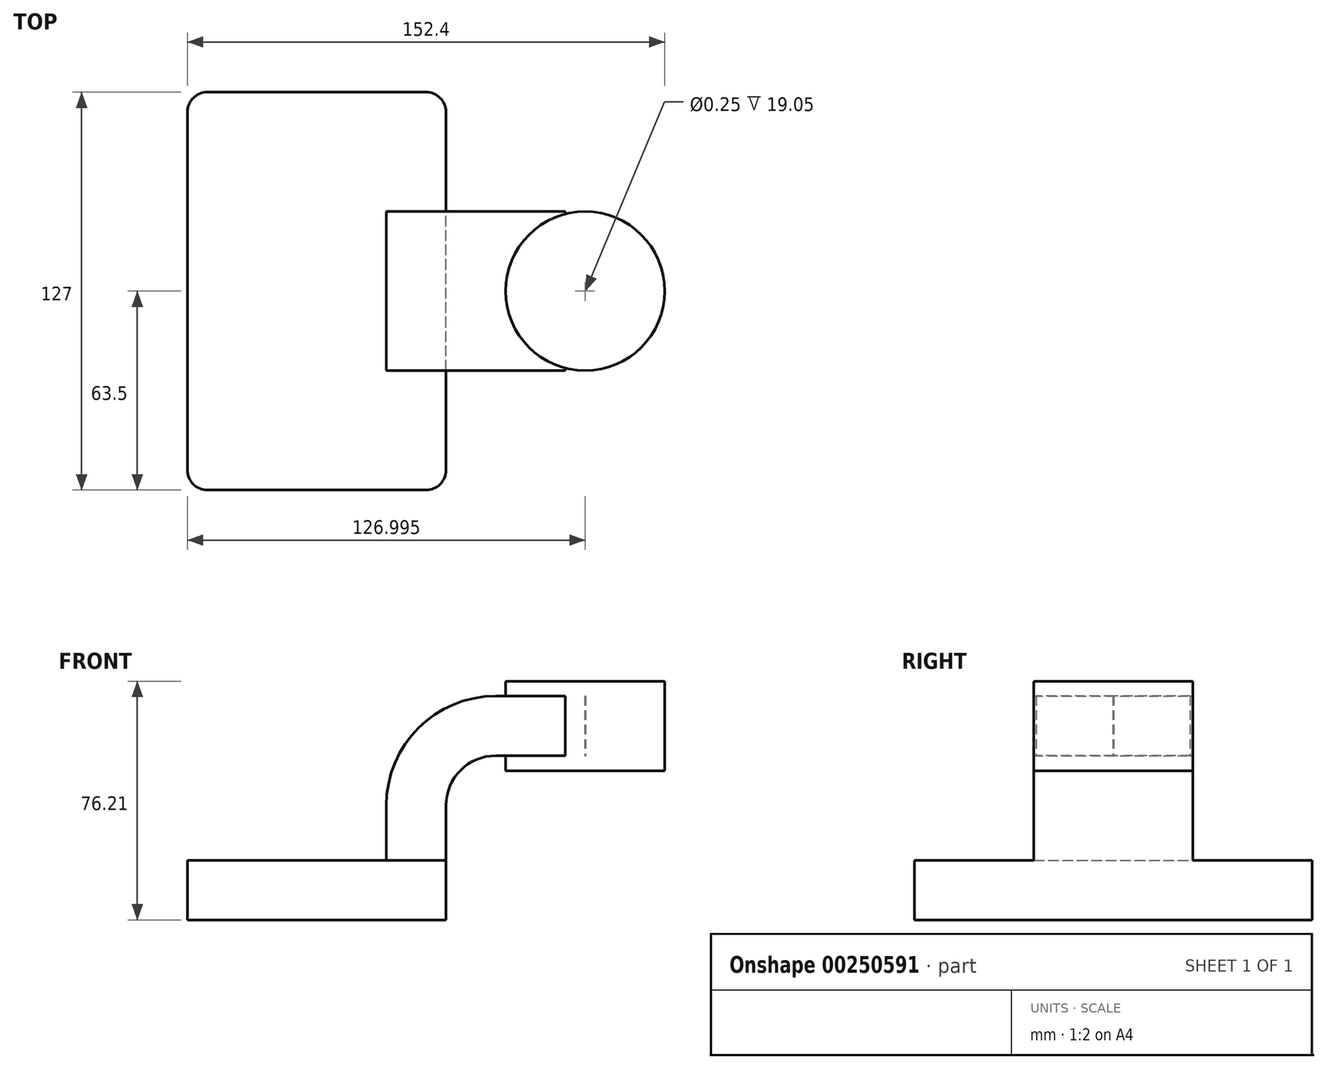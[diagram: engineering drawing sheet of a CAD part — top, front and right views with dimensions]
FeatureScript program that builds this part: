
annotation { "Feature Type Name" : "Feature", "Feature Type Description" : "" }
export const myFeature = defineFeature(function(context is Context, id is Id, definition is map)
    precondition{}
    {
        {
            var Q0;
            Q0=qCreatedBy(makeId("Front.planeOp"),FACE);
            var sketch = newSketch(context, id + "F0", { "sketchPlane" : qUnion([Q0])});
            skLineSegment(sketch, "E0.bottom", {"start": v(41.27, 9.53) * mm, "end": v(-41.28, 9.53) * mm});
            skLineSegment(sketch, "E0.top", {"start": v(41.28, -9.52) * mm, "end": v(-41.27, -9.52) * mm});
            skLineSegment(sketch, "E0.left", {"start": v(41.28, 9.53) * mm, "end": v(41.28, -9.52) * mm});
            skLineSegment(sketch, "E0.right", {"start": v(-41.28, 9.53) * mm, "end": v(-41.27, -9.52) * mm});
            skPoint(sketch, "E0.middle", {"position": v(0, 0) * mm});
            skLineSegment(sketch, "E1.bottom", {"start": v(111.12, 66.68) * mm, "end": v(60.32, 66.68) * mm});
            skLineSegment(sketch, "E1.top", {"start": v(111.12, 38.1) * mm, "end": v(60.33, 38.1) * mm});
            skLineSegment(sketch, "E1.left", {"start": v(111.12, 66.68) * mm, "end": v(111.12, 38.1) * mm});
            skLineSegment(sketch, "E1.right", {"start": v(60.32, 66.68) * mm, "end": v(60.33, 38.1) * mm});
            skPoint(sketch, "E1.middle", {"position": v(85.73, 52.39) * mm});
            skLineSegment(sketch, "E2", {"start": v(41.27, 9.53) * mm, "end": v(41.27, 27) * mm});
            skArc(sketch, "E3", {"start": v(41.27, 27) * mm, "mid": v(45.92, 38.23) * mm, "end": v(57.15, 42.88) * mm});
            skLineSegment(sketch, "E4", {"start": v(57.15, 42.88) * mm, "end": v(85.85, 42.88) * mm});
            skLineSegment(sketch, "E5.0", {"start": v(57.15, 61.93) * mm, "end": v(85.85, 61.93) * mm});
            skArc(sketch, "E5.1", {"start": v(22.23, 27) * mm, "mid": v(32.45, 51.7) * mm, "end": v(57.15, 61.93) * mm});
            skLineSegment(sketch, "E5.2", {"start": v(22.23, 9.53) * mm, "end": v(22.23, 27) * mm});
            skLineSegment(sketch, "E6", {"start": v(85.85, 42.88) * mm, "end": v(85.85, 61.93) * mm});
            skFitSpline(sketch, "E7", {"points": [v(-41.28, 9.52) * mm, v(57.15, 61.93) * mm], "startDerivative": vector(3.53, 68.47) * mm, "endDerivative": vector(154.22, 0.04) * mm});
            skLineSegment(sketch, "E8", {"start": v(85.72, 38.1) * mm, "end": v(85.72, 66.68) * mm});
            skSolve(sketch);
        }
        {
            var Q0;
            Q0=makeQuery(id+"F0.imprint","IMPRINT",FACE,{"disambiguationData":[TD([[makeQuery(id+"F0.imprint","IMPRINT",EDGE,{"derivedFrom":sQuery(id+"F0.wireOp",EDGE,"E0.top")}),-1.0]])]});
            extrude(context, id + "F1", {"entities" : qUnion([Q0]), "endBound" : BoundingType.SYMMETRIC, "depth" : 127 * mm});
        }
        {
            var Q0;
            {var subQ1=sQuery(id+"F0.wireOp",EDGE,"E2");Q0=makeQuery(id+"F0.imprint","IMPRINT",FACE,{"disambiguationData":[TD([[makeQuery(id+"F0.imprint","IMPRINT",EDGE,{"derivedFrom":subQ1}),1.0]])]});}
            extrude(context, id + "F2", {"entities" : qUnion([Q0]), "operationType" : NewBodyOperationType.ADD, "endBound" : BoundingType.SYMMETRIC, "depth" : 50.8 * mm});
        }
        {
            var Q0;
            Q0=makeQuery(id+"F0.imprint","IMPRINT",FACE,{"disambiguationData":[TD([[makeQuery(id+"F0.imprint","IMPRINT",EDGE,{"derivedFrom":sQuery(id+"F0.wireOp",EDGE,"E5.1")}),1.0]])]});
            extrude(context, id + "F3", {"entities" : qUnion([Q0]), "operationType" : NewBodyOperationType.ADD, "endBound" : BoundingType.SYMMETRIC, "depth" : 15.88 * mm});
        }
        {
            var Q0;
            Q0=makeQuery(id+"F1.opExtrude","CAP_EDGE",EDGE,{"disambiguationData":[OSD([sQuery(id+"F0.wireOp",EDGE,"E0.left")])],"isStart":false});
            var Q1;
            Q1=makeQuery(id+"F1.opExtrude","CAP_EDGE",EDGE,{"disambiguationData":[OSD([sQuery(id+"F0.wireOp",EDGE,"E0.right")])],"isStart":false});
            var Q2;
            Q2=makeQuery(id+"F1.opExtrude","CAP_EDGE",EDGE,{"disambiguationData":[OSD([sQuery(id+"F0.wireOp",EDGE,"E0.left")])],"isStart":true});
            var Q3;
            Q3=makeQuery(id+"F1.opExtrude","CAP_EDGE",EDGE,{"disambiguationData":[OSD([sQuery(id+"F0.wireOp",EDGE,"E0.right")])],"isStart":true});
            fillet(context, id + "F4", {"entities" : qUnion([Q0, Q1, Q2, Q3]), "radius" : 6.35 * mm, "tangentPropagation" : true, "allowEdgeOverflow" : false});
        }
        {
            var Q0;
            Q0=makeQuery(id+"F2.opExtrude","SWEPT_FACE",FACE,{"disambiguationData":[OSD([sQuery(id+"F0.wireOp",EDGE,"E1.right")])]});
            extrude(context, id + "F5", {"entities" : qUnion([Q0]), "operationType" : NewBodyOperationType.ADD, "depth" : 19.05 * mm});
        }
        {
            var Q0;
            {var subQ4=sQuery(id+"F0.wireOp",EDGE,"E1.left");Q0=makeQuery(id+"F0.imprint","IMPRINT",FACE,{"disambiguationData":[TD([[makeQuery(id+"F0.imprint","IMPRINT",EDGE,{"derivedFrom":subQ4}),-1.0]])]});}
            var Q1;
            Q1=sQuery(id+"F0.wireOp",EDGE,"E8");
            revolve(context, id + "F6", {"operationType" : NewBodyOperationType.ADD, "entities" : qUnion([Q0]), "axis" : qUnion([Q1]), "revolveType" : RevolveType.FULL});
        }
    });
